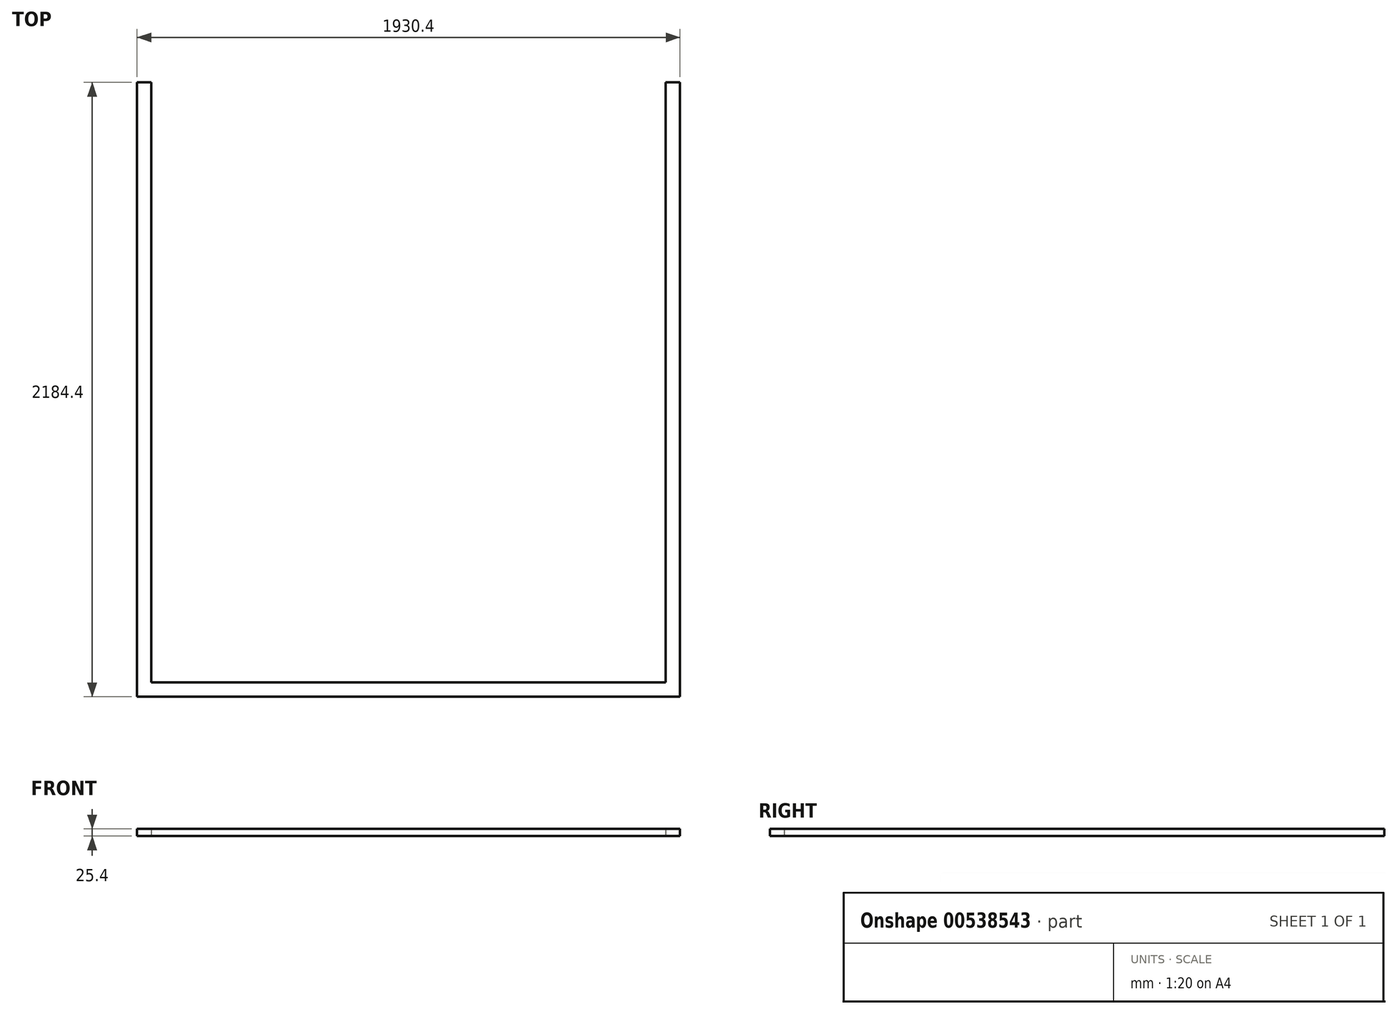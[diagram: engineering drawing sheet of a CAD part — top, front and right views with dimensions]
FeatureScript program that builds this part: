
annotation { "Feature Type Name" : "Feature", "Feature Type Description" : "" }
export const myFeature = defineFeature(function(context is Context, id is Id, definition is map)
    precondition{}
    {
        {
            var Q0;
            Q0=qCreatedBy(makeId("Top.planeOp"),FACE);
            var sketch = newSketch(context, id + "F0", { "sketchPlane" : qUnion([Q0])});
            skLineSegment(sketch, "E0.top", {"start": v(-914.4, -1066.8) * mm, "end": v(914.4, -1066.8) * mm});
            skLineSegment(sketch, "E0.left", {"start": v(-914.4, 1066.8) * mm, "end": v(-914.4, -1066.8) * mm});
            skLineSegment(sketch, "E0.right", {"start": v(914.4, 1066.8) * mm, "end": v(914.4, -1066.8) * mm});
            skPoint(sketch, "E0.middle", {"position": v(0, 0) * mm});
            skLineSegment(sketch, "E1.top", {"start": v(-965.2, -1117.6) * mm, "end": v(965.2, -1117.6) * mm});
            skLineSegment(sketch, "E1.left", {"start": v(-965.2, 1066.8) * mm, "end": v(-965.2, -1117.6) * mm});
            skLineSegment(sketch, "E1.right", {"start": v(965.2, 1066.8) * mm, "end": v(965.2, -1117.6) * mm});
            skLineSegment(sketch, "E2", {"start": v(-914.4, 1066.8) * mm, "end": v(-965.2, 1066.8) * mm});
            skLineSegment(sketch, "E3", {"start": v(914.4, 1066.8) * mm, "end": v(965.2, 1066.8) * mm});
            skPoint(sketch, "E1.bottom.start.orphan", {"position": v(-965.2, 1117.6) * mm});
            skPoint(sketch, "E4.orphan", {"position": v(965.2, 1117.6) * mm});
            skSolve(sketch);
        }
        {
            var Q0;
            Q0=makeQuery(id+"F0.imprint","IMPRINT",FACE,{"disambiguationData":[TD([[makeQuery(id+"F0.imprint","IMPRINT",EDGE,{"derivedFrom":sQuery(id+"F0.wireOp",EDGE,"E0.top")}),-1.0]])]});
            extrude(context, id + "F1", {"entities" : qUnion([Q0]), "depth" : 25.4 * mm, "offsetDistance" : 25.4 * mm});
        }
    });
